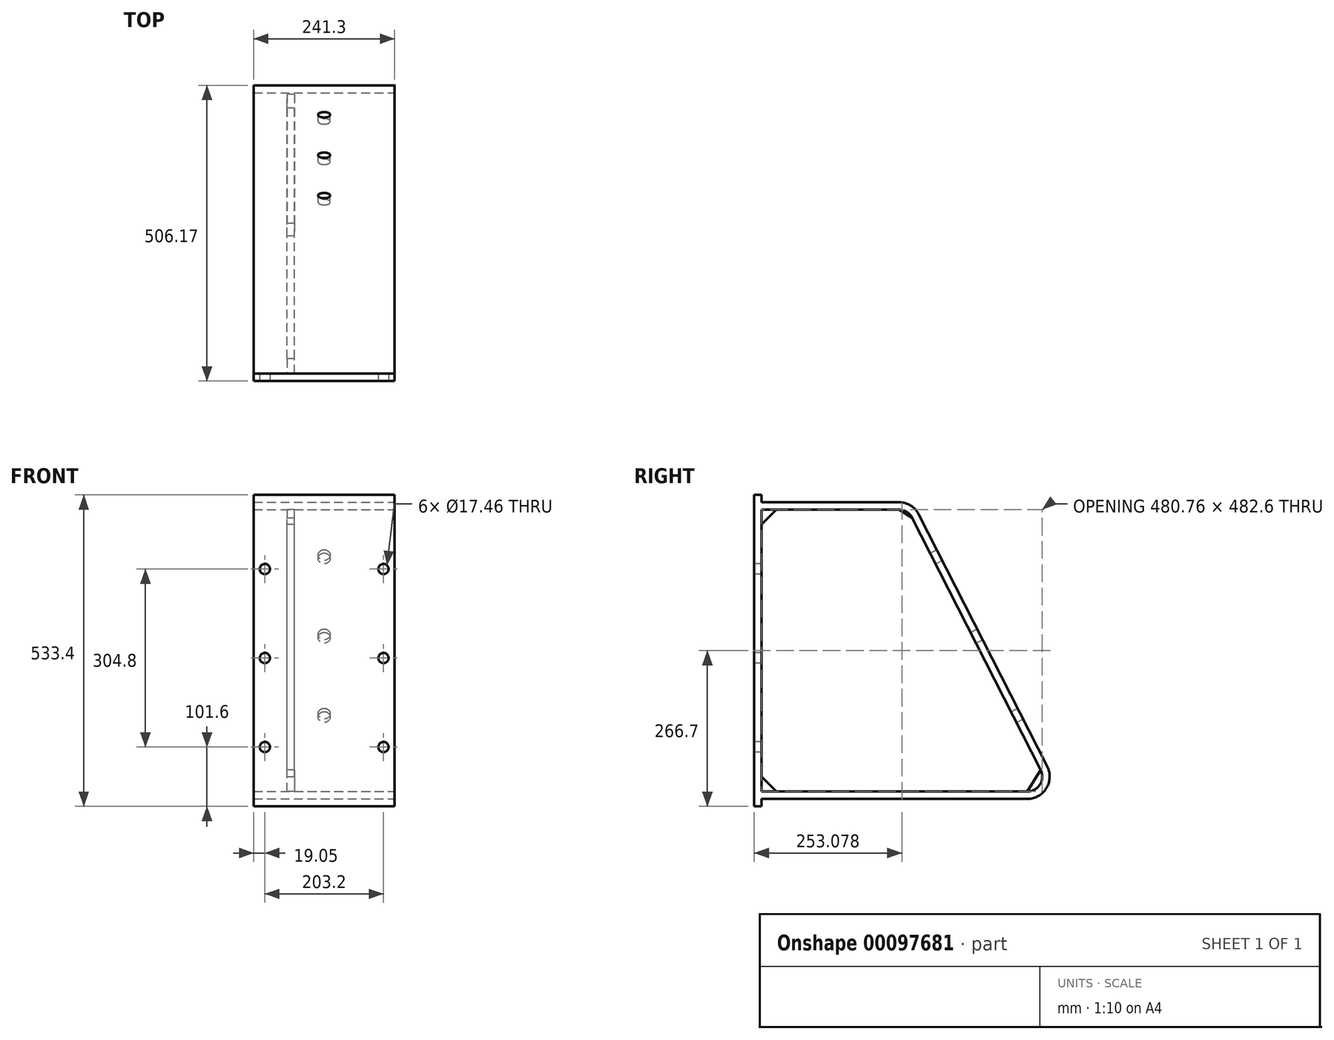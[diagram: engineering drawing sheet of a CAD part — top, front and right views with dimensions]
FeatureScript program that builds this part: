
annotation { "Feature Type Name" : "Feature", "Feature Type Description" : "" }
export const myFeature = defineFeature(function(context is Context, id is Id, definition is map)
    precondition{}
    {
        {
            var Q0;
            Q0=qCreatedBy(makeId("Right.planeOp"),FACE);
            var sketch = newSketch(context, id + "F0", { "sketchPlane" : qUnion([Q0])});
            skLineSegment(sketch, "E0.bottom", {"start": v(0, 0) * mm, "end": v(496.82, 0) * mm});
            skLineSegment(sketch, "E0.top", {"start": v(0, 482.6) * mm, "end": v(250.93, 482.6) * mm});
            skLineSegment(sketch, "E0.left", {"start": v(0, 0) * mm, "end": v(0, 482.6) * mm});
            skLineSegment(sketch, "E1", {"start": v(496.82, 0) * mm, "end": v(250.93, 482.6) * mm});
            skSolve(sketch);
        }
        {
            var Q0;
            Q0 = qSketchRegion(id + "F0", true);
            extrude(context, id + "F1", {"entities" : qUnion([Q0]), "endBound" : BoundingType.SYMMETRIC, "depth" : 12.7 * mm});
        }
        {
            var Q0;
            Q0=makeQuery(id+"F1.opExtrude","SWEPT_EDGE",EDGE,{"disambiguationData":[OSD([sQuery(id+"F0.wireOp",EDGE,"E0.top"),sQuery(id+"F0.wireOp",EDGE,"E1")])]});
            var Q1;
            Q1=makeQuery(id+"F1.opExtrude","SWEPT_EDGE",EDGE,{"disambiguationData":[OSD([sQuery(id+"F0.wireOp",EDGE,"E0.top"),sQuery(id+"F0.wireOp",EDGE,"E0.left")])]});
            var Q2;
            Q2=makeQuery(id+"F1.opExtrude","SWEPT_EDGE",EDGE,{"disambiguationData":[OSD([sQuery(id+"F0.wireOp",EDGE,"E0.bottom"),sQuery(id+"F0.wireOp",EDGE,"E0.left")])]});
            var Q3;
            Q3=makeQuery(id+"F1.opExtrude","SWEPT_EDGE",EDGE,{"disambiguationData":[OSD([sQuery(id+"F0.wireOp",EDGE,"E0.bottom"),sQuery(id+"F0.wireOp",EDGE,"E1")])]});
            chamfer(context, id + "F2", {"entities" : qUnion([Q0, Q1, Q2, Q3]), "width" : 25.4 * mm, "tangentPropagation" : true});
        }
        {
            var Q0;
            Q0=makeQuery(id+"F1.opExtrude","CAP_FACE",FACE,{"disambiguationData":[OSD([sQuery(id+"F0.wireOp",EDGE,"E0.bottom"),sQuery(id+"F0.wireOp",EDGE,"E0.top"),sQuery(id+"F0.wireOp",EDGE,"E0.left"),sQuery(id+"F0.wireOp",EDGE,"E1")])],"isStart":false});
            cPlane(context, id + "F3", {"entities" : qUnion([Q0]), "cplaneType" : CPlaneType.OFFSET, "offset" : 171.45 * mm, "width" : 152.4 * mm, "height" : 152.4 * mm});
        }
        {
            var Q0;
            Q0=qCreatedBy(id+"F3.planeOp",FACE);
            var sketch = newSketch(context, id + "F4", { "sketchPlane" : qUnion([Q0])});
            skLineSegment(sketch, "E2.0", {"start": v(0, -25.4) * mm, "end": v(0, 508) * mm});
            skLineSegment(sketch, "E3.0", {"start": v(0, 0) * mm, "end": v(455.37, 0) * mm});
            skLineSegment(sketch, "E4.0", {"start": v(478, 36.93) * mm, "end": v(258, 468.73) * mm});
            skLineSegment(sketch, "E5.0", {"start": v(0, 482.6) * mm, "end": v(235.36, 482.6) * mm});
            skPoint(sketch, "E6.orphan", {"position": v(0, 441.15) * mm});
            skPoint(sketch, "E7.orphan", {"position": v(0, 41.45) * mm});
            skPoint(sketch, "E8.orphan", {"position": v(41.45, 0) * mm});
            skLineSegment(sketch, "E9.0", {"start": v(-12.7, -25.4) * mm, "end": v(0, -25.4) * mm});
            skLineSegment(sketch, "E10.0", {"start": v(-12.7, -25.4) * mm, "end": v(-12.7, 508) * mm});
            skLineSegment(sketch, "E11.0", {"start": v(-12.7, 508) * mm, "end": v(0, 508) * mm});
            skPoint(sketch, "E12.orphan", {"position": v(41.45, 482.6) * mm});
            skPoint(sketch, "E13.orphan", {"position": v(225.53, 482.6) * mm});
            skPoint(sketch, "E14.orphan", {"position": v(262.46, 459.97) * mm});
            skPoint(sketch, "E15.orphan", {"position": v(466.12, 60.27) * mm});
            skPoint(sketch, "E16.orphan", {"position": v(429.19, 0) * mm});
            skPoint(sketch, "E17.visualSharp", {"position": v(496.82, 0) * mm});
            skArc(sketch, "E17.filletArc", {"start": v(455.37, 0) * mm, "mid": v(477.03, 12.13) * mm, "end": v(478, 36.93) * mm});
            skArc(sketch, "E18.filletArc", {"start": v(258, 468.73) * mm, "mid": v(248.63, 478.86) * mm, "end": v(235.36, 482.6) * mm});
            skLineSegment(sketch, "E19.0", {"start": v(0, -12.7) * mm, "end": v(455.37, -12.7) * mm});
            skLineSegment(sketch, "E19.1", {"start": v(0, 495.3) * mm, "end": v(235.36, 495.3) * mm});
            skArc(sketch, "E19.2", {"start": v(269.3, 474.5) * mm, "mid": v(255.27, 489.69) * mm, "end": v(235.36, 495.3) * mm});
            skLineSegment(sketch, "E19.3", {"start": v(489.32, 42.7) * mm, "end": v(269.3, 474.5) * mm});
            skArc(sketch, "E19.4", {"start": v(455.37, -12.7) * mm, "mid": v(487.86, 5.5) * mm, "end": v(489.32, 42.7) * mm});
            skSolve(sketch);
        }
        {
            var Q0;
            Q0 = qSketchRegion(id + "F4", true);
            extrude(context, id + "F5", {"entities" : qUnion([Q0]), "operationType" : NewBodyOperationType.ADD, "oppositeDirection" : true, "depth" : 241.3 * mm});
        }
        {
            var Q0;
            Q0=makeQuery(id+"F5.opExtrude","SWEPT_FACE",FACE,{"disambiguationData":[OSD([sQuery(id+"F4.wireOp",EDGE,"E10.0")])]});
            var sketch = newSketch(context, id + "F6", { "sketchPlane" : qUnion([Q0])});
            skLineSegment(sketch, "E20.0", {"start": v(-63.5, 482.6) * mm, "end": v(177.8, 482.6) * mm, "construction": true});
            skLineSegment(sketch, "E21.0", {"start": v(-63.5, 508) * mm, "end": v(177.8, 508) * mm, "construction": true});
            skLineSegment(sketch, "E22", {"start": v(57.15, 508) * mm, "end": v(57.15, 76.2) * mm, "construction": true});
            skLineSegment(sketch, "E23.0", {"start": v(-63.5, 381) * mm, "end": v(177.8, 381) * mm, "construction": true});
            skLineSegment(sketch, "E24.0", {"start": v(-63.5, 228.6) * mm, "end": v(177.8, 228.6) * mm, "construction": true});
            skLineSegment(sketch, "E25.0", {"start": v(-63.5, 76.2) * mm, "end": v(177.8, 76.2) * mm, "construction": true});
            skLineSegment(sketch, "E26.0", {"start": v(-44.45, 508) * mm, "end": v(-44.45, 76.2) * mm, "construction": true});
            skLineSegment(sketch, "E27.0", {"start": v(158.75, 508) * mm, "end": v(158.75, 76.2) * mm, "construction": true});
            skPoint(sketch, "E28", {"position": v(-44.45, 381) * mm});
            skPoint(sketch, "E29", {"position": v(-44.45, 228.6) * mm});
            skPoint(sketch, "E30", {"position": v(-44.45, 76.2) * mm});
            skPoint(sketch, "E31", {"position": v(158.75, 76.2) * mm});
            skPoint(sketch, "E32", {"position": v(158.75, 228.6) * mm});
            skPoint(sketch, "E33", {"position": v(158.75, 381) * mm});
            skSolve(sketch);
        }
        {
            var Q0;
            Q0=sQuery(id+"F6.wireOp",VERTEX,"E28");
            var Q1;
            Q1=sQuery(id+"F6.wireOp",VERTEX,"E33");
            var Q2;
            Q2=sQuery(id+"F6.wireOp",VERTEX,"E29");
            var Q3;
            Q3=sQuery(id+"F6.wireOp",VERTEX,"E32");
            var Q4;
            Q4=sQuery(id+"F6.wireOp",VERTEX,"E30");
            var Q5;
            Q5=sQuery(id+"F6.wireOp",VERTEX,"E31");
            var Q6;
            Q6=makeQuery(id+"F1.opExtrude","SWEPT_BODY",BODY,{"disambiguationData":[OSD([sQuery(id+"F0.wireOp",EDGE,"E0.bottom"),sQuery(id+"F0.wireOp",EDGE,"E0.top"),sQuery(id+"F0.wireOp",EDGE,"E0.left"),sQuery(id+"F0.wireOp",EDGE,"E1")])]});
            hole(context, id + "F7", {"style" : HoleStyle.SIMPLE, "endStyle" : HoleEndStyle.BLIND, "holeDiameter" : 17.46 * mm, "holeDepth" : 25.4 * mm, "locations" : qUnion([Q0, Q1, Q2, Q3, Q4, Q5]), "scope" : qUnion([Q6])});
        }
        {
            var Q0;
            Q0=makeQuery(id+"F1.opExtrude","CAP_FACE",FACE,{"disambiguationData":[OSD([sQuery(id+"F0.wireOp",EDGE,"E0.bottom"),sQuery(id+"F0.wireOp",EDGE,"E0.top"),sQuery(id+"F0.wireOp",EDGE,"E0.left"),sQuery(id+"F0.wireOp",EDGE,"E1")])],"isStart":false});
            var sketch = newSketch(context, id + "F8", { "sketchPlane" : qUnion([Q0])});
            skLineSegment(sketch, "E34.0", {"start": v(517.55, -12.7) * mm, "end": v(502.88, 16.08) * mm});
            skLineSegment(sketch, "E35.0", {"start": v(0, -12.7) * mm, "end": v(455.37, -12.7) * mm, "construction": true});
            skPoint(sketch, "E36.orphan", {"position": v(489.32, 42.7) * mm});
            skPoint(sketch, "E37.orphan", {"position": v(455.37, -12.7) * mm});
            skLineSegment(sketch, "E38", {"start": v(502.88, 16.08) * mm, "end": v(490.55, -12.7) * mm});
            skLineSegment(sketch, "E39.trimOffspring", {"start": v(489.32, 42.7) * mm, "end": v(269.3, 474.5) * mm, "construction": true});
            skLineSegment(sketch, "E40.trimOffspring", {"start": v(490.55, -12.7) * mm, "end": v(517.55, -12.7) * mm});
            skSolve(sketch);
        }
        {
            var Q0;
            Q0=makeQuery(id+"F8.imprint","IMPRINT",FACE,{"disambiguationData":[TD([[makeQuery(id+"F8.imprint","IMPRINT",EDGE,{"derivedFrom":sQuery(id+"F8.wireOp",EDGE,"E34.0")}),1.0]])]});
            extrude(context, id + "F9", {"entities" : qUnion([Q0]), "depth" : 25.4 * mm});
        }
        {
            var Q0;
            Q0=makeQuery(id+"F5.opExtrude","SWEPT_FACE",FACE,{"disambiguationData":[OSD([sQuery(id+"F4.wireOp",EDGE,"E19.3")])]});
            var sketch = newSketch(context, id + "F10", { "sketchPlane" : qUnion([Q0])});
            skLineSegment(sketch, "E41.0", {"start": v(-269.39, -246.28) * mm, "end": v(273.48, -246.28) * mm, "construction": true});
            skPoint(sketch, "E42.orphan", {"position": v(-31.75, -246.28) * mm});
            skPoint(sketch, "E43.orphan", {"position": v(-6.35, -246.28) * mm});
            skLineSegment(sketch, "E44", {"start": v(63.5, -222.2) * mm, "end": v(-177.8, -222.2) * mm, "construction": true});
            skLineSegment(sketch, "E45", {"start": v(-57.15, -222.2) * mm, "end": v(-57.15, 496.96) * mm, "construction": true});
            skPoint(sketch, "E45.endSnap0", {"position": v(-57.15, -184.1) * mm});
            skLineSegment(sketch, "E46.0", {"start": v(-269.39, -82.45) * mm, "end": v(273.48, -82.45) * mm, "construction": true});
            skLineSegment(sketch, "E47.0", {"start": v(-269.39, 69.95) * mm, "end": v(273.48, 69.95) * mm, "construction": true});
            skLineSegment(sketch, "E48.0", {"start": v(-269.39, 222.35) * mm, "end": v(273.48, 222.35) * mm, "construction": true});
            skPoint(sketch, "E49", {"position": v(-57.15, 222.35) * mm});
            skPoint(sketch, "E50", {"position": v(-57.15, 69.95) * mm});
            skPoint(sketch, "E51", {"position": v(-57.15, -82.45) * mm});
            skSolve(sketch);
        }
        {
            var Q0;
            Q0=sQuery(id+"F10.wireOp",VERTEX,"E49");
            var Q1;
            Q1=sQuery(id+"F10.wireOp",VERTEX,"E50");
            var Q2;
            Q2=sQuery(id+"F10.wireOp",VERTEX,"E51");
            var Q3;
            Q3=makeQuery(id+"F1.opExtrude","SWEPT_BODY",BODY,{"disambiguationData":[OSD([sQuery(id+"F0.wireOp",EDGE,"E0.bottom"),sQuery(id+"F0.wireOp",EDGE,"E0.top"),sQuery(id+"F0.wireOp",EDGE,"E0.left"),sQuery(id+"F0.wireOp",EDGE,"E1")])]});
            hole(context, id + "F11", {"style" : HoleStyle.SIMPLE, "endStyle" : HoleEndStyle.BLIND, "holeDiameter" : 20.64 * mm, "holeDepth" : 25.4 * mm, "locations" : qUnion([Q0, Q1, Q2]), "scope" : qUnion([Q3])});
        }
        {
            var Q0;
            Q0=makeQuery(id+"F9.opExtrude","SWEPT_BODY",BODY,{"disambiguationData":[OSD([sQuery(id+"F8.wireOp",EDGE,"E34.0"),sQuery(id+"F8.wireOp",EDGE,"E38"),sQuery(id+"F8.wireOp",EDGE,"E40.trimOffspring")])]});
            deleteBodies(context, id + "F12", {"entities" : qUnion([Q0])});
        }
    });
